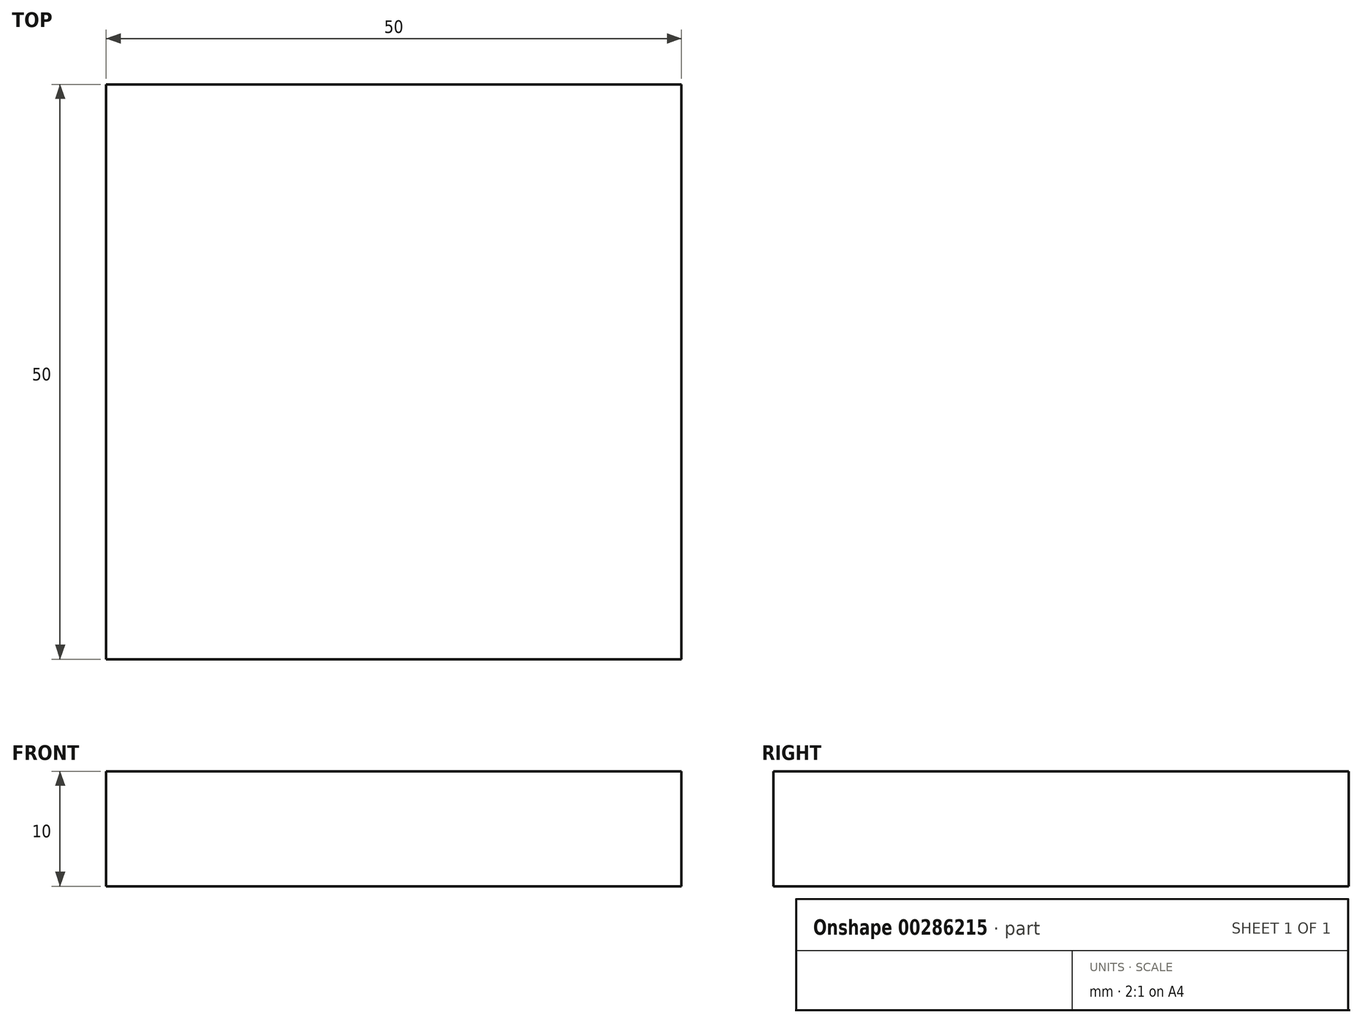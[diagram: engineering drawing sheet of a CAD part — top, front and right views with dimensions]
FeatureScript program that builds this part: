
annotation { "Feature Type Name" : "Feature", "Feature Type Description" : "" }
export const myFeature = defineFeature(function(context is Context, id is Id, definition is map)
    precondition{}
    {
        {
            var Q0;
            Q0=qCreatedBy(makeId("Top.planeOp"),FACE);
            var sketch = newSketch(context, id + "F0", { "sketchPlane" : qUnion([Q0])});
            skLineSegment(sketch, "E0.bottom", {"start": v(25, -25) * mm, "end": v(-25, -25) * mm});
            skLineSegment(sketch, "E0.top", {"start": v(25, 25) * mm, "end": v(-25, 25) * mm});
            skLineSegment(sketch, "E0.left", {"start": v(25, -25) * mm, "end": v(25, 25) * mm});
            skLineSegment(sketch, "E0.right", {"start": v(-25, -25) * mm, "end": v(-25, 25) * mm});
            skPoint(sketch, "E0.middle", {"position": v(0, 0) * mm});
            skSolve(sketch);
        }
        {
            var Q0;
            Q0 = qSketchRegion(id + "F0", true);
            extrude(context, id + "F1", {"entities" : qUnion([Q0]), "oppositeDirection" : true, "depth" : 10 * mm});
        }
    });
